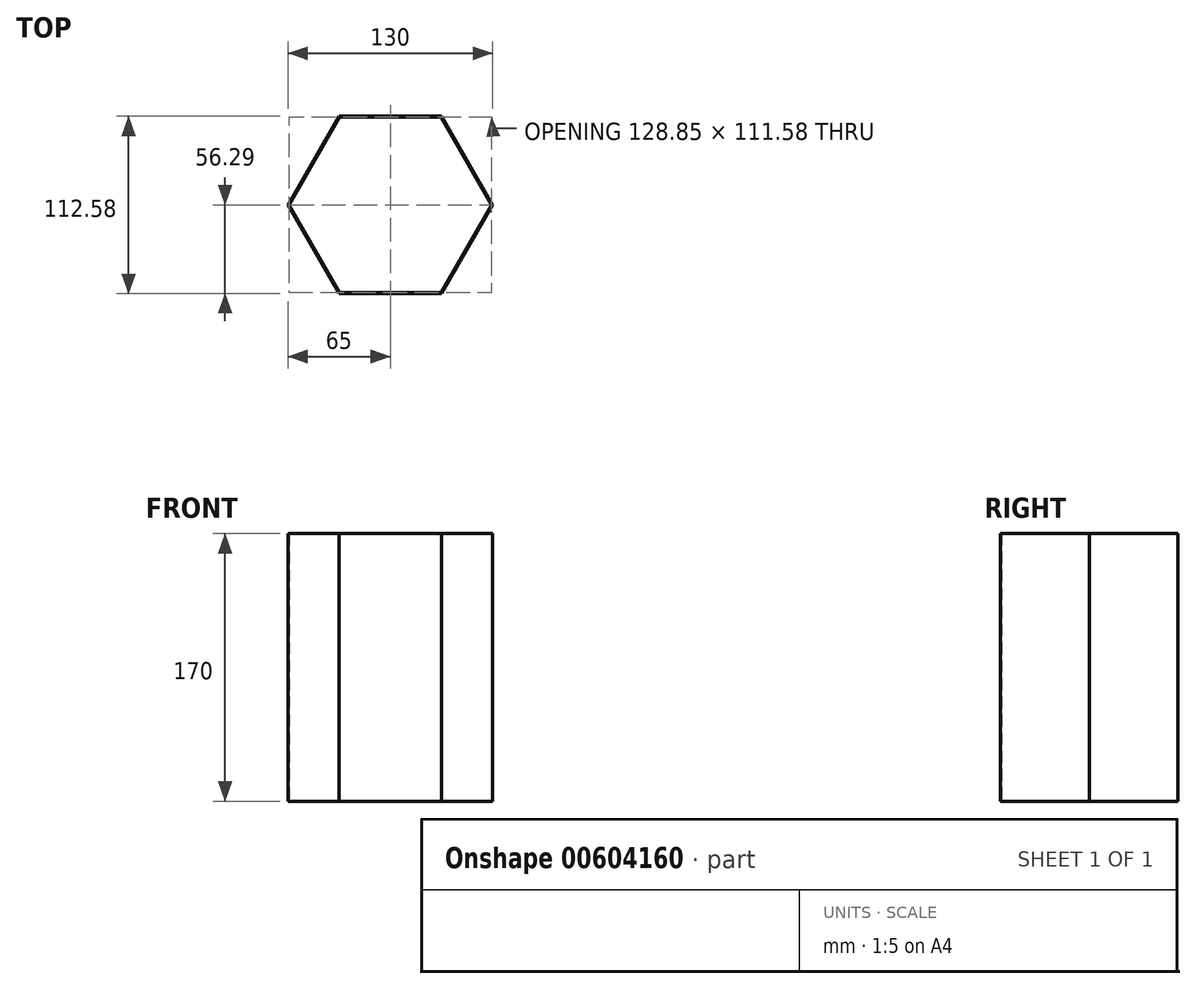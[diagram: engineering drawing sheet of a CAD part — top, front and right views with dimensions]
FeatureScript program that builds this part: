
annotation { "Feature Type Name" : "Feature", "Feature Type Description" : "" }
export const myFeature = defineFeature(function(context is Context, id is Id, definition is map)
    precondition{}
    {
        {
            var Q0;
            Q0=qCreatedBy(makeId("Top.planeOp"),FACE);
            var sketch = newSketch(context, id + "F0", { "sketchPlane" : qUnion([Q0])});
            skCircle(sketch, "E0.cCircle", {"center": v(0, 0) * mm, "radius": 56.3 * mm, "construction": true});
            skLineSegment(sketch, "E0.0", {"start": v(32.5, 56.3) * mm, "end": v(65, 0) * mm});
            skLineSegment(sketch, "E0.1", {"start": v(65, 0) * mm, "end": v(32.5, -56.3) * mm});
            skLineSegment(sketch, "E0.2", {"start": v(32.5, -56.3) * mm, "end": v(-32.5, -56.3) * mm});
            skLineSegment(sketch, "E0.3", {"start": v(-32.5, -56.3) * mm, "end": v(-65, 0) * mm});
            skLineSegment(sketch, "E0.4", {"start": v(-65, 0) * mm, "end": v(-32.5, 56.3) * mm});
            skLineSegment(sketch, "E0.5", {"start": v(-32.5, 56.3) * mm, "end": v(32.5, 56.3) * mm});
            skPoint(sketch, "E0.0.midPoint", {"position": v(48.75, 28.15) * mm});
            skCircle(sketch, "E1.cCircle", {"center": v(0, 0) * mm, "radius": 55.8 * mm, "construction": true});
            skLineSegment(sketch, "E1.0", {"start": v(64.42, 0) * mm, "end": v(32.21, -55.8) * mm});
            skLineSegment(sketch, "E1.1", {"start": v(32.21, -55.8) * mm, "end": v(-32.21, -55.8) * mm});
            skLineSegment(sketch, "E1.2", {"start": v(-32.21, -55.8) * mm, "end": v(-64.42, 0) * mm});
            skLineSegment(sketch, "E1.3", {"start": v(-64.42, 0) * mm, "end": v(-32.21, 55.8) * mm});
            skLineSegment(sketch, "E1.4", {"start": v(-32.21, 55.8) * mm, "end": v(32.21, 55.8) * mm});
            skLineSegment(sketch, "E1.5", {"start": v(32.21, 55.8) * mm, "end": v(64.42, 0) * mm});
            skPoint(sketch, "E1.0.midPoint", {"position": v(48.32, -27.9) * mm});
            skSolve(sketch);
        }
        {
            var Q0;
            Q0 = qSketchRegion(id + "F0", true);
            extrude(context, id + "F1", {"entities" : qUnion([Q0]), "depth" : 170 * mm, "offsetDistance" : 25 * mm});
        }
    });
